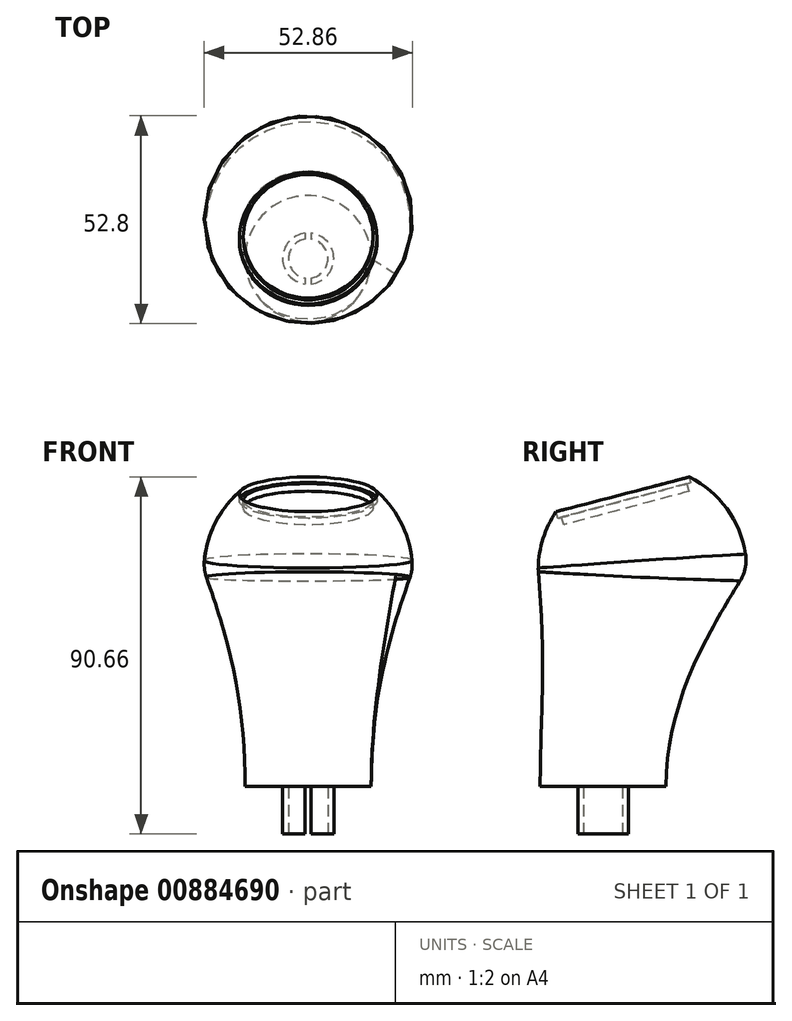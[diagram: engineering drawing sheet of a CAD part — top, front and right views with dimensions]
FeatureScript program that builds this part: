
annotation { "Feature Type Name" : "Feature", "Feature Type Description" : "" }
export const myFeature = defineFeature(function(context is Context, id is Id, definition is map)
    precondition{}
    {
        {
            var Q0;
            Q0=qCreatedBy(makeId("Top.planeOp"),FACE);
            var sketch = newSketch(context, id + "F0", { "sketchPlane" : qUnion([Q0])});
            skCircle(sketch, "E0", {"center": v(0, 0) * mm, "radius": 5 * mm});
            skCircle(sketch, "E1", {"center": v(0, 0) * mm, "radius": 6.5 * mm});
            skLineSegment(sketch, "E2.left", {"start": v(-0.75, 6.46) * mm, "end": v(-0.75, 4.94) * mm});
            skLineSegment(sketch, "E2.right", {"start": v(0.75, 6.46) * mm, "end": v(0.75, 4.94) * mm});
            skLineSegment(sketch, "E3.trimOffspring", {"start": v(0.75, -4.94) * mm, "end": v(0.75, -6.46) * mm});
            skLineSegment(sketch, "E4.trimOffspring", {"start": v(-0.75, -4.94) * mm, "end": v(-0.75, -6.46) * mm});
            skSolve(sketch);
        }
        {
            var Q0;
            {var subQ0=sQuery(id+"F0.wireOp",EDGE,"E2.left");Q0=makeQuery(id+"F0.imprint","IMPRINT",FACE,{"disambiguationData":[TD([[makeQuery(id+"F0.imprint","IMPRINT",EDGE,{"derivedFrom":subQ0}),-1.0]])]});}
            var Q1;
            {var subQ0=sQuery(id+"F0.wireOp",EDGE,"E2.right");Q1=makeQuery(id+"F0.imprint","IMPRINT",FACE,{"disambiguationData":[TD([[makeQuery(id+"F0.imprint","IMPRINT",EDGE,{"derivedFrom":subQ0}),1.0]])]});}
            extrude(context, id + "F1", {"entities" : qUnion([Q0, Q1]), "depth" : 12 * mm, "offsetDistance" : 25 * mm});
        }
        {
            var Q0;
            Q0=makeQuery(id+"F1.opExtrude","CAP_FACE",FACE,{"disambiguationData":[OSD([sQuery(id+"F0.wireOp",EDGE,"E0"),sQuery(id+"F0.wireOp",EDGE,"E1"),sQuery(id+"F0.wireOp",EDGE,"E2.left"),sQuery(id+"F0.wireOp",EDGE,"E4.trimOffspring")])],"isStart":false});
            cPlane(context, id + "F2", {"entities" : qUnion([Q0]), "cplaneType" : CPlaneType.OFFSET, "offset" : 0 * mm, "width" : 150 * mm, "height" : 150 * mm});
        }
        {
            var Q0;
            Q0=qCreatedBy(id+"F2.planeOp",FACE);
            var sketch = newSketch(context, id + "F3", { "sketchPlane" : qUnion([Q0])});
            skCircle(sketch, "E5", {"center": v(0, 0) * mm, "radius": 16 * mm});
            skSolve(sketch);
        }
        {
            var Q0;
            Q0=makeQuery(id+"F3.imprint","IMPRINT",FACE,{"disambiguationData":[TD([[makeQuery(id+"F3.imprint","IMPRINT",EDGE,{"derivedFrom":sQuery(id+"F3.wireOp",EDGE,"E5")}),1.0]])]});
            cPlane(context, id + "F4", {"entities" : qUnion([Q0]), "cplaneType" : CPlaneType.OFFSET, "offset" : 55 * mm, "width" : 150 * mm, "height" : 150 * mm});
        }
        {
            var Q0;
            Q0=qCreatedBy(id+"F4.planeOp",FACE);
            var sketch = newSketch(context, id + "F5", { "sketchPlane" : qUnion([Q0])});
            skCircle(sketch, "E6", {"center": v(0, 10) * mm, "radius": 26.5 * mm});
            skSolve(sketch);
        }
        {
            var Q0;
            Q0=makeQuery(id+"F3.imprint","IMPRINT",FACE,{"disambiguationData":[TD([[makeQuery(id+"F3.imprint","IMPRINT",EDGE,{"derivedFrom":sQuery(id+"F3.wireOp",EDGE,"E5")}),1.0]])]});
            var Q1;
            Q1=makeQuery(id+"F5.imprint","IMPRINT",FACE,{"disambiguationData":[TD([[makeQuery(id+"F5.imprint","IMPRINT",EDGE,{"derivedFrom":sQuery(id+"F5.wireOp",EDGE,"E6")}),1.0]])]});
            loft(context, id + "F6", {"operationType" : NewBodyOperationType.ADD, "startCondition" : LoftEndDerivativeType.NORMAL_TO_PROFILE, "startMagnitude" : 1, "sheetProfilesArray" : [{ "sheetProfileEntities" : qUnion([Q0]) }, { "sheetProfileEntities" : qUnion([Q1]) }]});
        }
        {
            var Q0;
            Q0=qCreatedBy(makeId("Right.planeOp"),FACE);
            var sketch = newSketch(context, id + "F7", { "sketchPlane" : qUnion([Q0])});
            skArc(sketch, "E7", {"start": v(10, 93.5) * mm, "mid": v(-8.74, 85.74) * mm, "end": v(-16.5, 67) * mm});
            skLineSegment(sketch, "E8", {"start": v(10, 93.5) * mm, "end": v(29.83, 93.5) * mm, "construction": true});
            skLineSegment(sketch, "E9", {"start": v(-16.5, 67) * mm, "end": v(-16.5, 54.5) * mm, "construction": true});
            skLineSegment(sketch, "E10", {"start": v(10, 67) * mm, "end": v(10, 113.72) * mm, "construction": true});
            skLineSegment(sketch, "E11", {"start": v(10, 93.5) * mm, "end": v(10, 67) * mm});
            skLineSegment(sketch, "E12", {"start": v(-16.5, 67) * mm, "end": v(10, 67) * mm});
            skSolve(sketch);
        }
        {
            var Q0;
            Q0=makeQuery(id+"F7.imprint","IMPRINT",FACE,{"disambiguationData":[TD([[makeQuery(id+"F7.imprint","IMPRINT",EDGE,{"derivedFrom":sQuery(id+"F7.wireOp",EDGE,"E7")}),1.0]])]});
            var Q1;
            Q1=sQuery(id+"F7.wireOp",EDGE,"E10");
            revolve(context, id + "F8", {"operationType" : NewBodyOperationType.ADD, "surfaceOperationType" : NewSurfaceOperationType.NEW, "entities" : qUnion([Q0]), "axis" : qUnion([Q1]), "revolveType" : RevolveType.FULL});
        }
        {
            var Q0;
            Q0=makeQuery(id+"F8.boolean.opBoolean","MERGE",EDGE,{"derivedFrom":[makeQuery(id+"F6.opLoft","MID_CAP_EDGE",EDGE,{"disambiguationData":[OSD([sQuery(id+"F5.wireOp",EDGE,"E6")])],"capPos":1.0}),makeQuery(id+"F8.opRevolve","SWEPT_EDGE",EDGE,{"disambiguationData":[OSD([sQuery(id+"F7.wireOp",EDGE,"E7"),sQuery(id+"F7.wireOp",EDGE,"E12")])]})]});
            fillet(context, id + "F9", {"entities" : qUnion([Q0]), "radius" : 10 * mm, "tangentPropagation" : true, "allowEdgeOverflow" : false});
        }
        {
            var Q0;
            Q0=qCreatedBy(makeId("Right.planeOp"),FACE);
            var sketch = newSketch(context, id + "F10", { "sketchPlane" : qUnion([Q0])});
            skLineSegment(sketch, "E13", {"start": v(0, 0) * mm, "end": v(0, 113.33) * mm, "construction": true});
            skPoint(sketch, "E14", {"position": v(0, 91.54) * mm});
            skSolve(sketch);
        }
        {
            var Q0;
            Q0=qCreatedBy(makeId("Top.planeOp"),FACE);
            var Q1;
            Q1=sQuery(id+"F10.wireOp",VERTEX,"E14");
            cPlane(context, id + "F11", {"entities" : qUnion([Q0, Q1]), "cplaneType" : CPlaneType.PLANE_POINT, "offset" : 25 * mm, "width" : 150 * mm, "height" : 150 * mm});
        }
        {
            var Q0;
            Q0=qCreatedBy(id+"F11.planeOp",FACE);
            var sketch = newSketch(context, id + "F12", { "sketchPlane" : qUnion([Q0])});
            skLineSegment(sketch, "E15", {"start": v(0, 0) * mm, "end": v(47.58, 0) * mm, "construction": true});
            skSolve(sketch);
        }
        {
            var Q0;
            Q0=sQuery(id+"F12.wireOp",EDGE,"E15");
            cPlane(context, id + "F13", {"entities" : qUnion([Q0]), "cplaneType" : CPlaneType.LINE_ANGLE, "offset" : 25 * mm, "angle" : 75 * degree, "oppositeDirection" : true, "width" : 150 * mm, "height" : 150 * mm});
        }
        {
            var Q0;
            Q0=qCreatedBy(id+"F13.planeOp",FACE);
            var sketch = newSketch(context, id + "F14", { "sketchPlane" : qUnion([Q0])});
            skPoint(sketch, "E16", {"position": v(0, -27.15) * mm});
            skCircle(sketch, "E17", {"center": v(0, -27.15) * mm, "radius": 17.5 * mm});
            skCircle(sketch, "E18", {"center": v(0, -27.15) * mm, "radius": 16.5 * mm});
            skSolve(sketch);
        }
        {
            var Q0;
            Q0 = qSketchRegion(id + "F14", true);
            extrude(context, id + "F15", {"entities" : qUnion([Q0]), "operationType" : NewBodyOperationType.REMOVE, "depth" : 8 * mm, "offsetDistance" : 25 * mm, "hasSecondDirection" : true, "secondDirectionOppositeDirection" : true, "secondDirectionDepth" : 25 * mm});
        }
        {
            var Q0;
            Q0=makeQuery(id+"F14.imprint","IMPRINT",FACE,{"disambiguationData":[TD([[makeQuery(id+"F14.imprint","IMPRINT",EDGE,{"derivedFrom":sQuery(id+"F14.wireOp",EDGE,"E18")}),1.0]])]});
            extrude(context, id + "F16", {"entities" : qUnion([Q0]), "operationType" : NewBodyOperationType.REMOVE, "depth" : 10 * mm, "offsetDistance" : 25 * mm, "hasSecondDirection" : true, "secondDirectionOppositeDirection" : true, "secondDirectionDepth" : 25 * mm});
        }
    });
